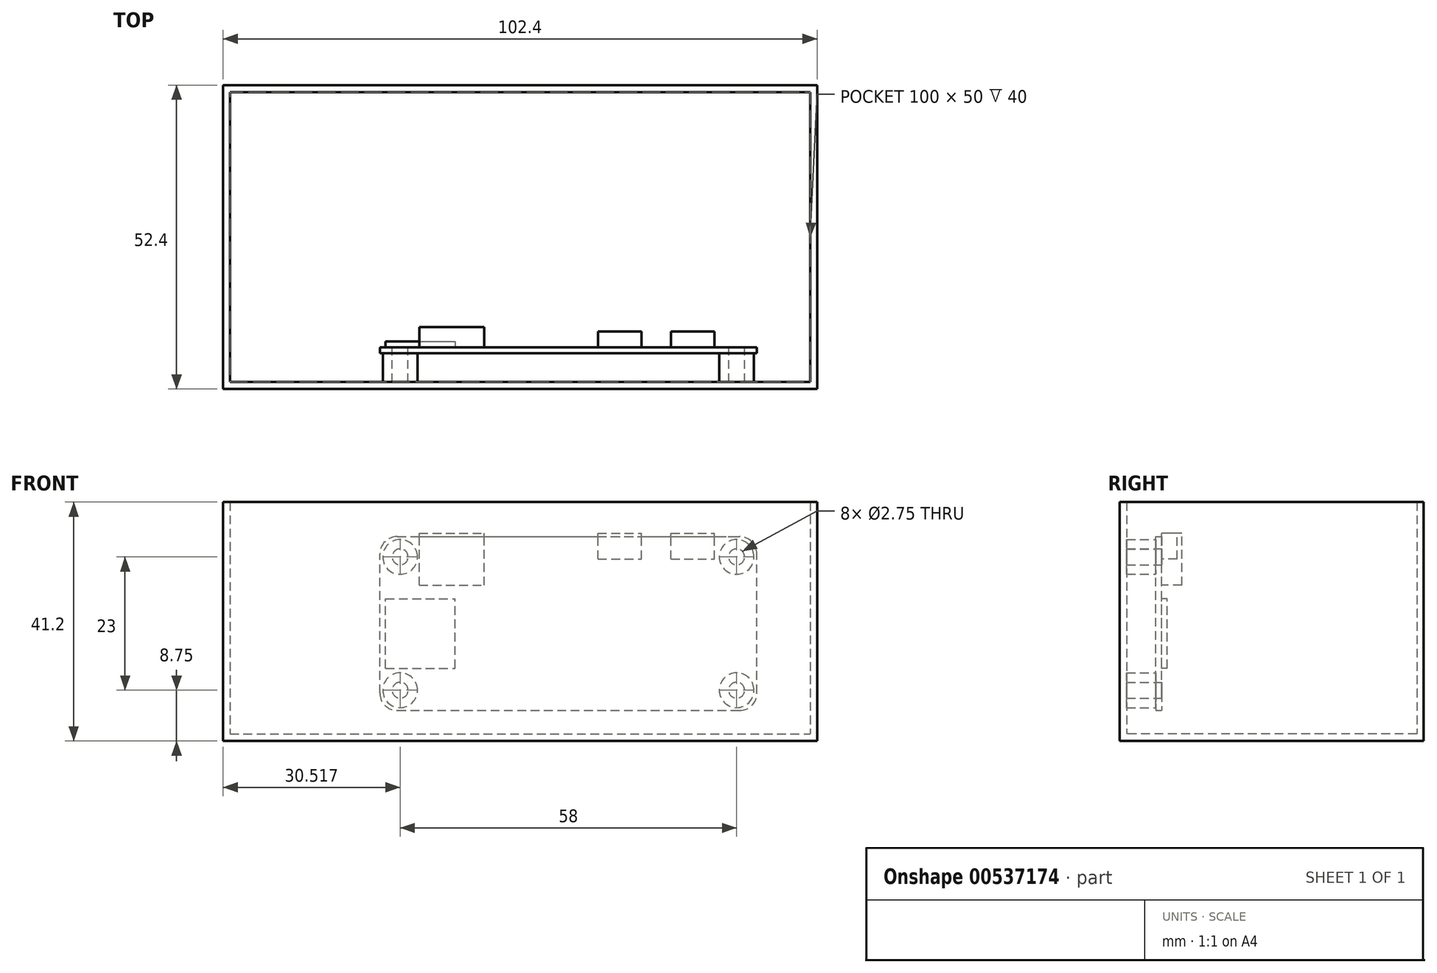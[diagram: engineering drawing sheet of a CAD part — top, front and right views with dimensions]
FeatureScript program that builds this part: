
annotation { "Feature Type Name" : "Feature", "Feature Type Description" : "" }
export const myFeature = defineFeature(function(context is Context, id is Id, definition is map)
    precondition{}
    {
        {
            var Q0;
            Q0=qCreatedBy(makeId("Top.planeOp"),FACE);
            var sketch = newSketch(context, id + "F0", { "sketchPlane" : qUnion([Q0])});
            skCircle(sketch, "E0", {"center": v(-33.23, 17.5) * mm, "radius": 1.38 * mm});
            skCircle(sketch, "E1", {"center": v(-33.23, 17.5) * mm, "radius": 3 * mm});
            skCircle(sketch, "E2", {"center": v(-33.23, -5.5) * mm, "radius": 1.38 * mm});
            skCircle(sketch, "E3", {"center": v(-33.23, -5.5) * mm, "radius": 3 * mm});
            skCircle(sketch, "E4", {"center": v(24.77, -5.5) * mm, "radius": 1.38 * mm});
            skCircle(sketch, "E5", {"center": v(24.77, -5.5) * mm, "radius": 3 * mm});
            skCircle(sketch, "E6", {"center": v(24.77, 17.5) * mm, "radius": 1.38 * mm});
            skCircle(sketch, "E7", {"center": v(24.77, 17.5) * mm, "radius": 3 * mm});
            skLineSegment(sketch, "E8.bottom", {"start": v(-33.73, 21) * mm, "end": v(25.27, 21) * mm});
            skLineSegment(sketch, "E8.top", {"start": v(-33.73, -9) * mm, "end": v(25.27, -9) * mm});
            skLineSegment(sketch, "E8.left", {"start": v(-36.73, 18) * mm, "end": v(-36.73, -6) * mm});
            skLineSegment(sketch, "E8.right", {"start": v(28.27, 18) * mm, "end": v(28.27, -6) * mm});
            skPoint(sketch, "E9.visualSharp", {"position": v(-36.73, 21) * mm});
            skArc(sketch, "E9.filletArc", {"start": v(-33.73, 21) * mm, "mid": v(-35.85, 20.12) * mm, "end": v(-36.73, 18) * mm});
            skPoint(sketch, "E10.visualSharp", {"position": v(28.27, 21) * mm});
            skArc(sketch, "E10.filletArc", {"start": v(28.27, 18) * mm, "mid": v(27.39, 20.12) * mm, "end": v(25.27, 21) * mm});
            skPoint(sketch, "E11.visualSharp", {"position": v(28.27, -9) * mm});
            skArc(sketch, "E11.filletArc", {"start": v(25.27, -9) * mm, "mid": v(27.39, -8.13) * mm, "end": v(28.27, -6) * mm});
            skPoint(sketch, "E12.visualSharp", {"position": v(-36.73, -9) * mm});
            skArc(sketch, "E12.filletArc", {"start": v(-36.73, -6) * mm, "mid": v(-35.85, -8.13) * mm, "end": v(-33.73, -9) * mm});
            skSolve(sketch);
        }
        {
            var Q0;
            Q0=makeQuery(id+"F0.imprint","IMPRINT",FACE,{"disambiguationData":[TD([[makeQuery(id+"F0.imprint","IMPRINT",EDGE,{"derivedFrom":sQuery(id+"F0.wireOp",EDGE,"E1")}),-1.0]])]});
            var Q1;
            {var subQ5=sQuery(id+"F0.wireOp",EDGE,"ccN6g2ZB-jOm5-5I2t-aCtq-MU3R8DTqx0pB.bottom");Q1=makeQuery(id+"F0.imprint","IMPRINT",FACE,{"disambiguationData":[TD([[makeQuery(id+"F0.imprint","IMPRINT",EDGE,{"derivedFrom":subQ5}),-1.0]])]});}
            var Q2;
            {var subQ5=sQuery(id+"F0.wireOp",EDGE,"2XHFnOv7-lSCR-7zIj-SoSe-tg8eTRICwzEZ.bottom");Q2=makeQuery(id+"F0.imprint","IMPRINT",FACE,{"disambiguationData":[TD([[makeQuery(id+"F0.imprint","IMPRINT",EDGE,{"derivedFrom":subQ5}),-1.0]])]});}
            var Q3;
            {var subQ5=sQuery(id+"F0.wireOp",EDGE,"MaF8rnOJ-xElN-91XC-iTwr-3nWo2MZqcvLa.bottom");Q3=makeQuery(id+"F0.imprint","IMPRINT",FACE,{"disambiguationData":[TD([[makeQuery(id+"F0.imprint","IMPRINT",EDGE,{"derivedFrom":subQ5}),-1.0]])]});}
            var Q4;
            Q4=makeQuery(id+"F0.imprint","IMPRINT",FACE,{"disambiguationData":[TD([[makeQuery(id+"F0.imprint","IMPRINT",EDGE,{"derivedFrom":sQuery(id+"F0.wireOp",EDGE,"E4")}),-1.0]])]});
            var Q5;
            Q5=makeQuery(id+"F0.imprint","IMPRINT",FACE,{"disambiguationData":[TD([[makeQuery(id+"F0.imprint","IMPRINT",EDGE,{"derivedFrom":sQuery(id+"F0.wireOp",EDGE,"E6")}),-1.0]])]});
            var Q6;
            Q6=makeQuery(id+"F0.imprint","IMPRINT",FACE,{"disambiguationData":[TD([[makeQuery(id+"F0.imprint","IMPRINT",EDGE,{"derivedFrom":sQuery(id+"F0.wireOp",EDGE,"E2")}),-1.0]])]});
            var Q7;
            Q7=makeQuery(id+"F0.imprint","IMPRINT",FACE,{"disambiguationData":[TD([[makeQuery(id+"F0.imprint","IMPRINT",EDGE,{"derivedFrom":sQuery(id+"F0.wireOp",EDGE,"E0")}),-1.0]])]});
            extrude(context, id + "F1", {"entities" : qUnion([Q0, Q1, Q2, Q3, Q4, Q5, Q6, Q7]), "oppositeDirection" : true, "depth" : 1 * mm, "offsetDistance" : 25 * mm});
        }
        {
            var Q0;
            Q0=makeQuery(id+"F1.opExtrude","CAP_FACE",FACE,{"disambiguationData":[OSD([sQuery(id+"F0.wireOp",EDGE,"E0"),sQuery(id+"F0.wireOp",EDGE,"E2"),sQuery(id+"F0.wireOp",EDGE,"E4"),sQuery(id+"F0.wireOp",EDGE,"E6"),sQuery(id+"F0.wireOp",EDGE,"E8.bottom"),sQuery(id+"F0.wireOp",EDGE,"E8.top"),sQuery(id+"F0.wireOp",EDGE,"E8.left"),sQuery(id+"F0.wireOp",EDGE,"E8.right"),sQuery(id+"F0.wireOp",EDGE,"E9.filletArc"),sQuery(id+"F0.wireOp",EDGE,"E10.filletArc"),sQuery(id+"F0.wireOp",EDGE,"E11.filletArc"),sQuery(id+"F0.wireOp",EDGE,"E12.filletArc")])],"isStart":true});
            var sketch = newSketch(context, id + "F2", { "sketchPlane" : qUnion([Q0])});
            skLineSegment(sketch, "E13.bottom", {"start": v(-35.73, 13.7) * mm, "end": v(-23.73, 13.7) * mm});
            skLineSegment(sketch, "E13.top", {"start": v(-35.73, 1.7) * mm, "end": v(-23.73, 1.7) * mm});
            skLineSegment(sketch, "E13.left", {"start": v(-35.73, 13.7) * mm, "end": v(-35.73, 1.7) * mm});
            skLineSegment(sketch, "E13.right", {"start": v(-23.73, 13.7) * mm, "end": v(-23.73, 1.7) * mm});
            skSolve(sketch);
        }
        {
            var Q0;
            Q0=makeQuery(id+"F2.imprint","IMPRINT",FACE,{"disambiguationData":[TD([[makeQuery(id+"F2.imprint","IMPRINT",EDGE,{"derivedFrom":sQuery(id+"F2.wireOp",EDGE,"E13.bottom")}),-1.0]])]});
            extrude(context, id + "F3", {"entities" : qUnion([Q0]), "operationType" : NewBodyOperationType.ADD, "depth" : 1 * mm, "offsetDistance" : 25 * mm});
        }
        {
            var Q0;
            Q0=makeQuery(id+"F1.opExtrude","CAP_FACE",FACE,{"disambiguationData":[OSD([sQuery(id+"F0.wireOp",EDGE,"E0"),sQuery(id+"F0.wireOp",EDGE,"E2"),sQuery(id+"F0.wireOp",EDGE,"E4"),sQuery(id+"F0.wireOp",EDGE,"E6"),sQuery(id+"F0.wireOp",EDGE,"E8.bottom"),sQuery(id+"F0.wireOp",EDGE,"E8.top"),sQuery(id+"F0.wireOp",EDGE,"E8.left"),sQuery(id+"F0.wireOp",EDGE,"E8.right"),sQuery(id+"F0.wireOp",EDGE,"E9.filletArc"),sQuery(id+"F0.wireOp",EDGE,"E10.filletArc"),sQuery(id+"F0.wireOp",EDGE,"E11.filletArc"),sQuery(id+"F0.wireOp",EDGE,"E12.filletArc")])],"isStart":true});
            var sketch = newSketch(context, id + "F4", { "sketchPlane" : qUnion([Q0])});
            skLineSegment(sketch, "E14.bottom", {"start": v(-29.93, -0.6) * mm, "end": v(-18.73, -0.6) * mm});
            skLineSegment(sketch, "E14.top", {"start": v(-29.93, -9.6) * mm, "end": v(-18.73, -9.6) * mm});
            skLineSegment(sketch, "E14.left", {"start": v(-29.93, -0.6) * mm, "end": v(-29.93, -9.6) * mm});
            skLineSegment(sketch, "E14.right", {"start": v(-18.73, -0.6) * mm, "end": v(-18.73, -9.6) * mm});
            skSolve(sketch);
        }
        {
            var Q0;
            Q0 = qSketchRegion(id + "F4", true);
            extrude(context, id + "F5", {"entities" : qUnion([Q0]), "operationType" : NewBodyOperationType.ADD, "depth" : 3.5 * mm, "offsetDistance" : 25 * mm});
        }
        {
            var Q0;
            Q0=makeQuery(id+"F1.opExtrude","CAP_FACE",FACE,{"disambiguationData":[OSD([sQuery(id+"F0.wireOp",EDGE,"E0"),sQuery(id+"F0.wireOp",EDGE,"E2"),sQuery(id+"F0.wireOp",EDGE,"E4"),sQuery(id+"F0.wireOp",EDGE,"E6"),sQuery(id+"F0.wireOp",EDGE,"E8.bottom"),sQuery(id+"F0.wireOp",EDGE,"E8.top"),sQuery(id+"F0.wireOp",EDGE,"E8.left"),sQuery(id+"F0.wireOp",EDGE,"E8.right"),sQuery(id+"F0.wireOp",EDGE,"E9.filletArc"),sQuery(id+"F0.wireOp",EDGE,"E10.filletArc"),sQuery(id+"F0.wireOp",EDGE,"E11.filletArc"),sQuery(id+"F0.wireOp",EDGE,"E12.filletArc")])],"isStart":true});
            var sketch = newSketch(context, id + "F6", { "sketchPlane" : qUnion([Q0])});
            skLineSegment(sketch, "E15.bottom", {"start": v(13.47, -5.1) * mm, "end": v(20.97, -5.1) * mm});
            skLineSegment(sketch, "E15.top", {"start": v(13.47, -9.6) * mm, "end": v(20.97, -9.6) * mm});
            skLineSegment(sketch, "E15.left", {"start": v(13.47, -5.1) * mm, "end": v(13.47, -9.6) * mm});
            skLineSegment(sketch, "E15.right", {"start": v(20.97, -5.1) * mm, "end": v(20.97, -9.6) * mm});
            skLineSegment(sketch, "E16.bottom", {"start": v(0.87, -5.1) * mm, "end": v(8.37, -5.1) * mm});
            skLineSegment(sketch, "E16.top", {"start": v(0.87, -9.6) * mm, "end": v(8.37, -9.6) * mm});
            skLineSegment(sketch, "E16.left", {"start": v(0.87, -5.1) * mm, "end": v(0.87, -9.6) * mm});
            skLineSegment(sketch, "E16.right", {"start": v(8.37, -5.1) * mm, "end": v(8.37, -9.6) * mm});
            skSolve(sketch);
        }
        {
            var Q0;
            Q0 = qSketchRegion(id + "F6", true);
            extrude(context, id + "F7", {"entities" : qUnion([Q0]), "operationType" : NewBodyOperationType.ADD, "depth" : 2.7 * mm, "offsetDistance" : 25 * mm});
        }
        {
            var Q0;
            Q0=makeQuery(id+"F1.opExtrude","CAP_FACE",FACE,{"disambiguationData":[OSD([sQuery(id+"F0.wireOp",EDGE,"E0"),sQuery(id+"F0.wireOp",EDGE,"E2"),sQuery(id+"F0.wireOp",EDGE,"E4"),sQuery(id+"F0.wireOp",EDGE,"E6"),sQuery(id+"F0.wireOp",EDGE,"E8.bottom"),sQuery(id+"F0.wireOp",EDGE,"E8.top"),sQuery(id+"F0.wireOp",EDGE,"E8.left"),sQuery(id+"F0.wireOp",EDGE,"E8.right"),sQuery(id+"F0.wireOp",EDGE,"E9.filletArc"),sQuery(id+"F0.wireOp",EDGE,"E10.filletArc"),sQuery(id+"F0.wireOp",EDGE,"E11.filletArc"),sQuery(id+"F0.wireOp",EDGE,"E12.filletArc")])],"isStart":false});
            var sketch = newSketch(context, id + "F8", { "sketchPlane" : qUnion([Q0])});
            skCircle(sketch, "E17", {"center": v(-33.23, 5.5) * mm, "radius": 1.38 * mm});
            skCircle(sketch, "E18", {"center": v(-33.23, 5.5) * mm, "radius": 3 * mm});
            skCircle(sketch, "E19", {"center": v(-33.23, -17.5) * mm, "radius": 1.38 * mm});
            skCircle(sketch, "E20", {"center": v(-33.23, -17.5) * mm, "radius": 3 * mm});
            skCircle(sketch, "E21", {"center": v(24.77, -17.5) * mm, "radius": 1.38 * mm});
            skCircle(sketch, "E22", {"center": v(24.77, -17.5) * mm, "radius": 3 * mm});
            skCircle(sketch, "E23", {"center": v(24.77, 5.5) * mm, "radius": 1.38 * mm});
            skCircle(sketch, "E24", {"center": v(24.77, 5.5) * mm, "radius": 3 * mm});
            skSolve(sketch);
        }
        {
            var Q0;
            Q0 = qSketchRegion(id + "F8", true);
            extrude(context, id + "F9", {"entities" : qUnion([Q0]), "depth" : 5 * mm, "offsetDistance" : 25 * mm});
        }
        {
            var Q0;
            Q0=makeQuery(id+"F1.opExtrude","CAP_EDGE",EDGE,{"disambiguationData":[OSD([sQuery(id+"F0.wireOp",EDGE,"E8.bottom")])],"isStart":true});
            cPoint(context, id + "F10", {"entities" : qUnion([Q0]), "parameter" : 0.5});
        }
        {
            var Q0;
            Q0=makeQuery(id+"F1.opExtrude","SWEPT_BODY",BODY,{"disambiguationData":[OSD([sQuery(id+"F0.wireOp",EDGE,"E0"),sQuery(id+"F0.wireOp",EDGE,"E2"),sQuery(id+"F0.wireOp",EDGE,"E4"),sQuery(id+"F0.wireOp",EDGE,"E6"),sQuery(id+"F0.wireOp",EDGE,"E8.bottom"),sQuery(id+"F0.wireOp",EDGE,"E8.top"),sQuery(id+"F0.wireOp",EDGE,"E8.left"),sQuery(id+"F0.wireOp",EDGE,"E8.right"),sQuery(id+"F0.wireOp",EDGE,"E9.filletArc"),sQuery(id+"F0.wireOp",EDGE,"E10.filletArc"),sQuery(id+"F0.wireOp",EDGE,"E11.filletArc"),sQuery(id+"F0.wireOp",EDGE,"E12.filletArc")])]});
            var Q1;
            Q1=makeQuery(id+"F9.opExtrude","SWEPT_BODY",BODY,{"disambiguationData":[OSD([sQuery(id+"F8.wireOp",EDGE,"E17"),sQuery(id+"F8.wireOp",EDGE,"E18")])]});
            var Q2;
            Q2=makeQuery(id+"F9.opExtrude","SWEPT_BODY",BODY,{"disambiguationData":[OSD([sQuery(id+"F8.wireOp",EDGE,"E23"),sQuery(id+"F8.wireOp",EDGE,"E24")])]});
            var Q3;
            Q3=makeQuery(id+"F9.opExtrude","SWEPT_BODY",BODY,{"disambiguationData":[OSD([sQuery(id+"F8.wireOp",EDGE,"E21"),sQuery(id+"F8.wireOp",EDGE,"E22")])]});
            var Q4;
            Q4=makeQuery(id+"F9.opExtrude","SWEPT_BODY",BODY,{"disambiguationData":[OSD([sQuery(id+"F8.wireOp",EDGE,"E19"),sQuery(id+"F8.wireOp",EDGE,"E20")])]});
            var Q5;
            Q5 = qCreatedBy(id + "F10" ,VERTEX);
            var Q6;
            Q6=makeQuery(id+"F1.opExtrude","CAP_EDGE",EDGE,{"disambiguationData":[OSD([sQuery(id+"F0.wireOp",EDGE,"E8.bottom")])],"isStart":true});
            transform(context, id + "F11", {"entities" : qUnion([Q0, Q1, Q2, Q3, Q4]), "transformType" : TransformType.ROTATION, "transformAxis" : qUnion([Q6]), "angle" : 270 * degree, "makeCopy" : false});
        }
        {
            var Q0;
            Q0=makeQuery(id+"F9.opExtrude","CAP_FACE",FACE,{"disambiguationData":[OSD([sQuery(id+"F8.wireOp",EDGE,"E17"),sQuery(id+"F8.wireOp",EDGE,"E18")])],"isStart":false});
            var sketch = newSketch(context, id + "F12", { "sketchPlane" : qUnion([Q0])});
            skLineSegment(sketch, "E25.bottom", {"start": v(-62.55, 35.95) * mm, "end": v(37.45, 35.95) * mm});
            skLineSegment(sketch, "E25.top", {"start": v(-62.55, -4.05) * mm, "end": v(37.45, -4.05) * mm});
            skLineSegment(sketch, "E25.left", {"start": v(-62.55, 35.95) * mm, "end": v(-62.55, -4.05) * mm});
            skLineSegment(sketch, "E25.right", {"start": v(37.45, 35.95) * mm, "end": v(37.45, -4.05) * mm});
            skSolve(sketch);
        }
        {
            var Q0;
            Q0 = qSketchRegion(id + "F12", true);
            extrude(context, id + "F13", {"entities" : qUnion([Q0]), "oppositeDirection" : true, "depth" : 50 * mm, "offsetDistance" : 25 * mm});
        }
        {
            var Q0;
            Q0=makeQuery(id+"F13.opExtrude","SWEPT_FACE",FACE,{"disambiguationData":[OSD([sQuery(id+"F12.wireOp",EDGE,"E25.bottom")])]});
            shell(context, id + "F14", {"entities" : qUnion([Q0]), "thickness" : 1.2 * mm, "oppositeDirection" : true});
        }
    });
